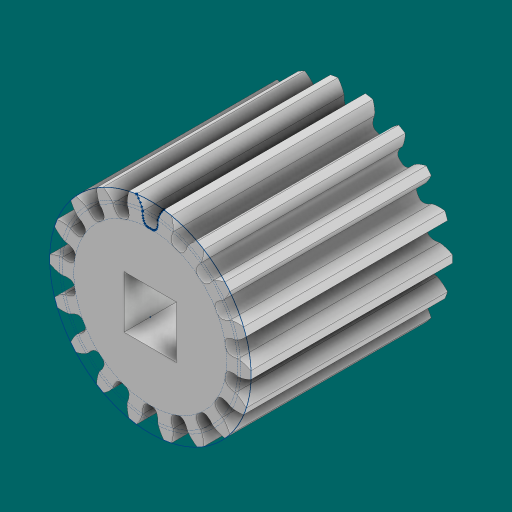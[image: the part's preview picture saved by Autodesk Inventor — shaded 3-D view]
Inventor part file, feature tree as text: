
AUTODESK INVENTOR PART (.ipt)
format: ipt  version: 2023.1 (Build 271208000, 208)  size: 812,544 bytes
history: native  units: in
note: dims shown in document units (in); Inventor stores cm internally (conversion verified against a paired STEP export)
features: extrude x5, sketch x4, pattern_circular x1, chamfer x1, projected_geometry x1
ambient origin geometry x8: Origin, YZ Plane, XZ Plane, XY Plane, X Axis, Y Axis, Z Axis, Center Point
bodies: Solid1 (feature_tree)
feature tree (12):
  sketch  "Sketch1"  dims[d0=1.0in d1=0.0in]
  extrude  "Extrusion1"  TaperAngle=0.0deg  [1 undecoded]
  extrude  "Extrusion2"  Depth=7.0866in TaperAngle=360.0deg
  pattern_circular  "Circular Pattern1"  [2 undecoded]
  extrude  "Extrusion3"  Depth=0.05in TaperAngle=0.0deg
  extrude  "Extrusion4"  Depth=0.05in
  extrude  "Extrusion5"  Depth=0.05in TaperAngle=0.0deg
  chamfer  "Chamfer2"  Distance=0.0118in Angle=45.0deg
  sketch  "Sketch2"  dims[d2=0.0in d3=0.0in d4=7.0866in d5=360.0deg]
  sketch  "Sketch3"  dims[d9=0.0in d10=0.0in]
  sketch  "Sketch4"  dims[d11=0.26in d12=0.26in d13=0.9in d14=0.0in d18=0.33in d19=0.05in d20=0.0in d21=0.0118in d22=0.125in d23=45.0deg d24=0.18in d25=0.18in]
  projected_geometry  "Projected Loop1"
note: 3 required parameter values undecoded (feature->parameter linkage not recoverable at this tier; creation-order binding heuristic only, values carry confidence <= 0.55)
